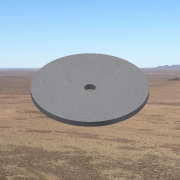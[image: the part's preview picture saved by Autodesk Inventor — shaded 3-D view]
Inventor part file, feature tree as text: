
AUTODESK INVENTOR PART (.ipt)
format: ipt  version: 2013 SP2 (Build 170200200, 200)  size: 142,848 bytes
history: native  units: in
note: dims shown in document units (in); Inventor stores cm internally (conversion verified against a paired STEP export)
features: extrude x1, sketch x1
ambient origin geometry x8: Origin, YZ Plane, XZ Plane, XY Plane, X Axis, Y Axis, Z Axis, Center Point
bodies: Solid1 (feature_tree)
feature tree (2):
  extrude  "Extrusion1"  Depth=1.0in
  sketch  "Sketch1"  dims[d0=10.0in d2=1.0in d3=0.5in d4=0.0in]
